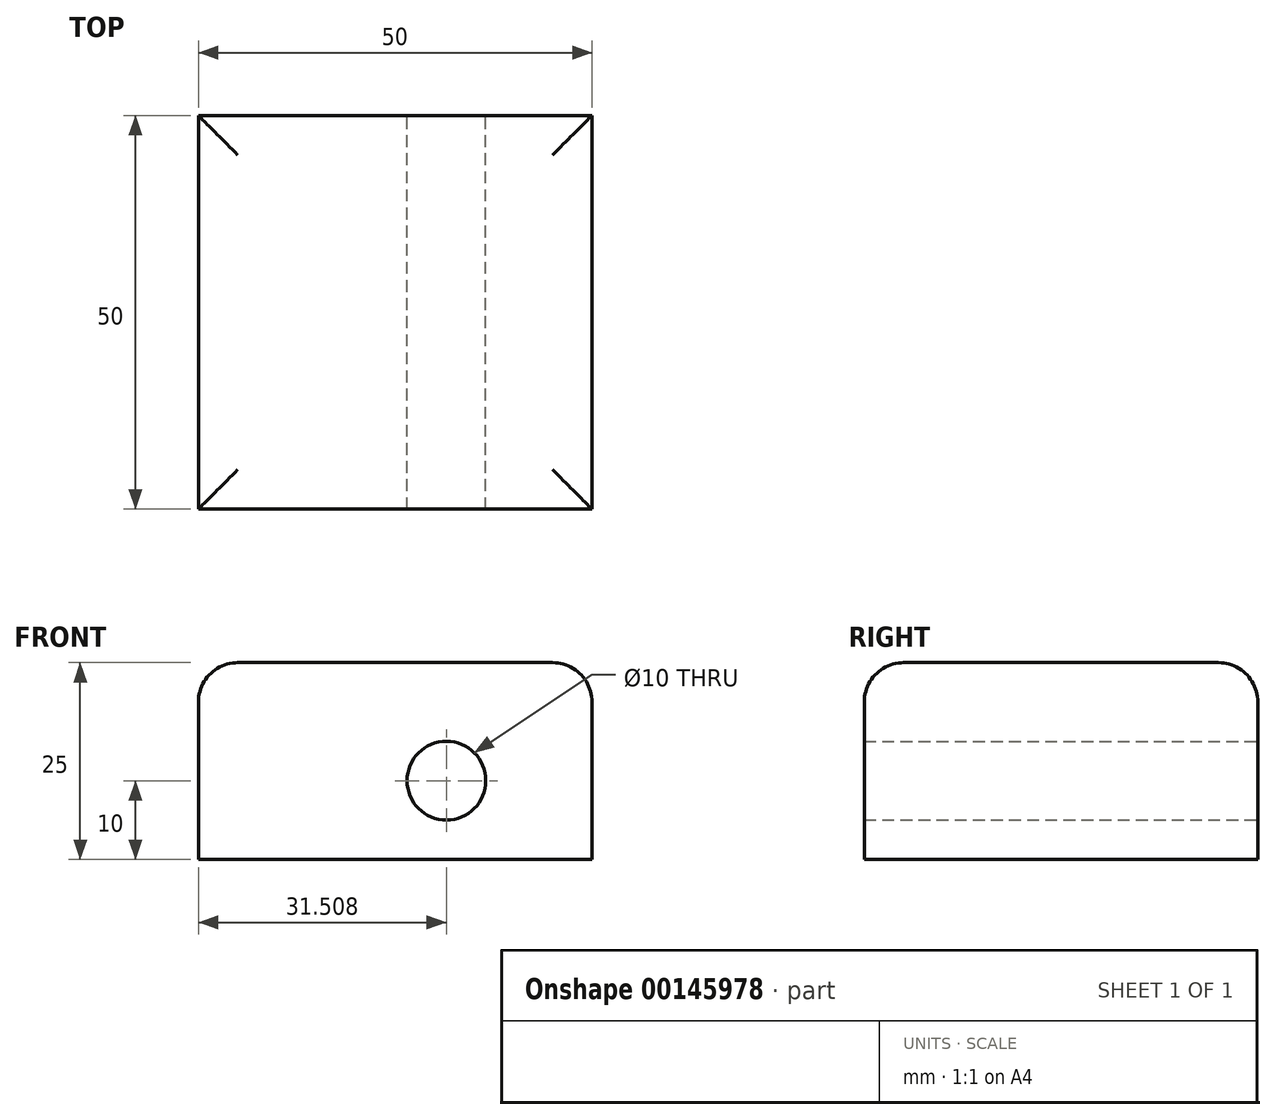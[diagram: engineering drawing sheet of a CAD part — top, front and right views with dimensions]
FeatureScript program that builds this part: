
annotation { "Feature Type Name" : "Feature", "Feature Type Description" : "" }
export const myFeature = defineFeature(function(context is Context, id is Id, definition is map)
    precondition{}
    {
        {
            var Q0;
            Q0=qCreatedBy(makeId("Front.planeOp"),FACE);
            var sketch = newSketch(context, id + "F0", { "sketchPlane" : qUnion([Q0])});
            skLineSegment(sketch, "E0.bottom", {"start": v(25, 12.5) * mm, "end": v(-25, 12.5) * mm});
            skLineSegment(sketch, "E0.top", {"start": v(25, -12.5) * mm, "end": v(-25, -12.5) * mm});
            skLineSegment(sketch, "E0.left", {"start": v(25, 12.5) * mm, "end": v(25, -12.5) * mm});
            skLineSegment(sketch, "E0.right", {"start": v(-25, 12.5) * mm, "end": v(-25, -12.5) * mm});
            skPoint(sketch, "E0.middle", {"position": v(0, 0) * mm});
            skSolve(sketch);
        }
        {
            var Q0;
            Q0=makeQuery(id+"F0.imprint","IMPRINT",FACE,{"disambiguationData":[TD([[makeQuery(id+"F0.imprint","IMPRINT",EDGE,{"derivedFrom":sQuery(id+"F0.wireOp",EDGE,"E0.bottom")}),1.0]])]});
            extrude(context, id + "F1", {"entities" : qUnion([Q0]), "oppositeDirection" : true, "depth" : 50 * mm});
        }
        {
            var Q0;
            Q0=makeQuery(id+"F1.opExtrude","SWEPT_EDGE",EDGE,{"disambiguationData":[OSD([sQuery(id+"F0.wireOp",EDGE,"E0.bottom"),sQuery(id+"F0.wireOp",EDGE,"E0.right")])]});
            var Q1;
            Q1=makeQuery(id+"F1.opExtrude","SWEPT_EDGE",EDGE,{"disambiguationData":[OSD([sQuery(id+"F0.wireOp",EDGE,"E0.bottom"),sQuery(id+"F0.wireOp",EDGE,"E0.left")])]});
            var Q2;
            Q2=makeQuery(id+"F1.opExtrude","CAP_EDGE",EDGE,{"disambiguationData":[OSD([sQuery(id+"F0.wireOp",EDGE,"E0.bottom")])],"isStart":true});
            var Q3;
            Q3=makeQuery(id+"F1.opExtrude","CAP_EDGE",EDGE,{"disambiguationData":[OSD([sQuery(id+"F0.wireOp",EDGE,"E0.bottom")])],"isStart":false});
            fillet(context, id + "F2", {"entities" : qUnion([Q0, Q1, Q2, Q3]), "radius" : 5 * mm, "tangentPropagation" : true, "allowEdgeOverflow" : false});
        }
        {
            var Q0;
            Q0=makeQuery(id+"F1.opExtrude","CAP_FACE",FACE,{"disambiguationData":[OSD([sQuery(id+"F0.wireOp",EDGE,"E0.bottom"),sQuery(id+"F0.wireOp",EDGE,"E0.top"),sQuery(id+"F0.wireOp",EDGE,"E0.left"),sQuery(id+"F0.wireOp",EDGE,"E0.right")])],"isStart":false});
            var sketch = newSketch(context, id + "F3", { "sketchPlane" : qUnion([Q0])});
            skCircle(sketch, "E1", {"center": v(-6.5, -2.5) * mm, "radius": 5 * mm});
            skPoint(sketch, "E1.centerSnap0", {"position": v(-25, -2.5) * mm});
            skSolve(sketch);
        }
        {
            var Q0;
            Q0=makeQuery(id+"F3.imprint","IMPRINT",FACE,{"disambiguationData":[TD([[makeQuery(id+"F3.imprint","IMPRINT",EDGE,{"derivedFrom":sQuery(id+"F3.wireOp",EDGE,"E1")}),1.0]])]});
            extrude(context, id + "F4", {"entities" : qUnion([Q0]), "operationType" : NewBodyOperationType.REMOVE, "endBound" : BoundingType.THROUGH_ALL, "oppositeDirection" : true, "depth" : 25 * mm});
        }
    });
